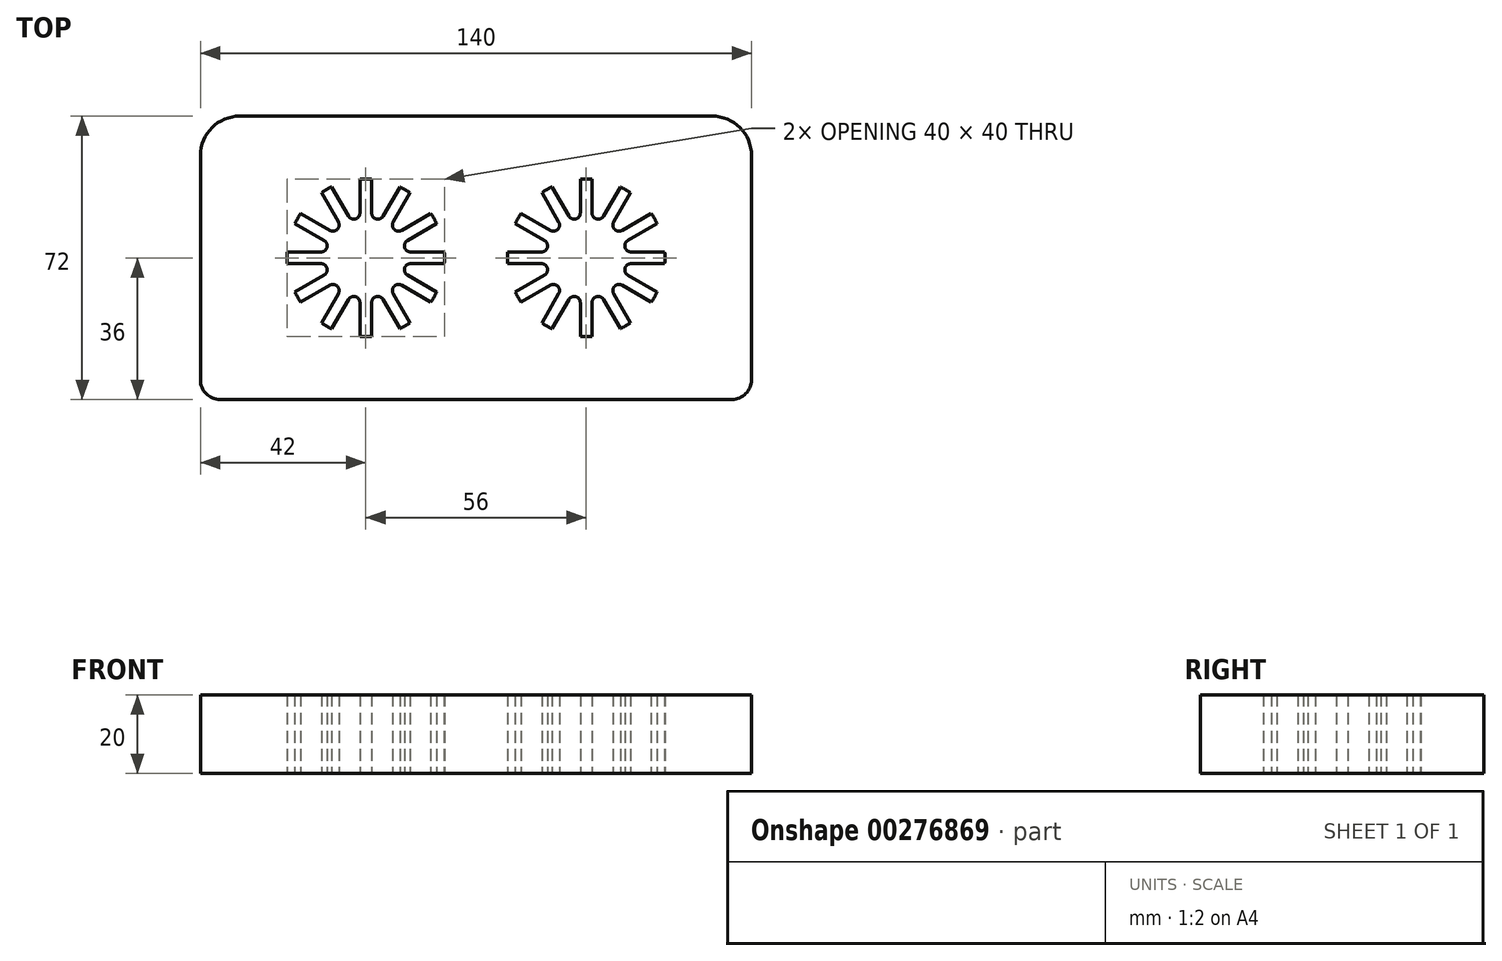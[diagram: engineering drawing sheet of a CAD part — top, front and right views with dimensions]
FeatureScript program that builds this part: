
annotation { "Feature Type Name" : "Feature", "Feature Type Description" : "" }
export const myFeature = defineFeature(function(context is Context, id is Id, definition is map)
    precondition{}
    {
        {
            var Q0;
            Q0=qCreatedBy(makeId("Top.planeOp"),FACE);
            var sketch = newSketch(context, id + "F0", { "sketchPlane" : qUnion([Q0])});
            skArc(sketch, "E0", {"start": v(-16.52, 11.27) * mm, "mid": v(-17.32, 10) * mm, "end": v(-18.02, 8.67) * mm});
            skArc(sketch, "E1", {"start": v(-6.35, 8) * mm, "mid": v(-7.23, 7.23) * mm, "end": v(-8, 6.35) * mm});
            skLineSegment(sketch, "E2", {"start": v(-19.94, -1.5) * mm, "end": v(-10.1, -1.5) * mm});
            skLineSegment(sketch, "E3", {"start": v(-20, 1.5) * mm, "end": v(-10.1, 1.5) * mm});
            skLineSegment(sketch, "E4", {"start": v(-18.02, 8.67) * mm, "end": v(-9.5, 3.76) * mm});
            skLineSegment(sketch, "E5", {"start": v(-16.52, 11.27) * mm, "end": v(-8, 6.35) * mm});
            skLineSegment(sketch, "E6", {"start": v(-1.5, 19.94) * mm, "end": v(-1.5, 10.1) * mm});
            skLineSegment(sketch, "E7", {"start": v(1.5, 19.94) * mm, "end": v(1.5, 10.1) * mm});
            skLineSegment(sketch, "E8", {"start": v(-8.42, 17.58) * mm, "end": v(-8.67, 18.02) * mm});
            skLineSegment(sketch, "E9", {"start": v(-8.67, 18.02) * mm, "end": v(-3.76, 9.5) * mm});
            skLineSegment(sketch, "E10", {"start": v(10.76, 15.64) * mm, "end": v(11.27, 16.52) * mm});
            skLineSegment(sketch, "E11", {"start": v(11.27, 16.52) * mm, "end": v(6.35, 8) * mm});
            skLineSegment(sketch, "E12", {"start": v(8.17, 17.14) * mm, "end": v(8.67, 18.02) * mm});
            skLineSegment(sketch, "E13", {"start": v(8.67, 18.02) * mm, "end": v(3.76, 9.5) * mm});
            skLineSegment(sketch, "E14", {"start": v(17.6, 8.43) * mm, "end": v(18.02, 8.67) * mm});
            skLineSegment(sketch, "E15", {"start": v(18.02, 8.67) * mm, "end": v(9.5, 3.76) * mm});
            skLineSegment(sketch, "E16", {"start": v(16.1, 11.03) * mm, "end": v(16.52, 11.27) * mm});
            skLineSegment(sketch, "E17", {"start": v(16.52, 11.27) * mm, "end": v(8, 6.35) * mm});
            skLineSegment(sketch, "E18", {"start": v(-10.8, 15.7) * mm, "end": v(-11.27, 16.52) * mm});
            skLineSegment(sketch, "E19", {"start": v(-10.8, 15.7) * mm, "end": v(-6.35, 8) * mm});
            skLineSegment(sketch, "E20.trimOffspring", {"start": v(-9.5, -3.76) * mm, "end": v(-18.02, -8.67) * mm});
            skLineSegment(sketch, "E21.trimOffspring", {"start": v(-8, -6.35) * mm, "end": v(-16.52, -11.27) * mm});
            skLineSegment(sketch, "E22.trimOffspring", {"start": v(-6.35, -8) * mm, "end": v(-11.27, -16.52) * mm});
            skLineSegment(sketch, "E23.trimOffspring", {"start": v(-3.76, -9.5) * mm, "end": v(-8.67, -18.02) * mm});
            skLineSegment(sketch, "E24.trimOffspring", {"start": v(-1.5, -10.1) * mm, "end": v(-1.5, -19.94) * mm});
            skLineSegment(sketch, "E25.trimOffspring", {"start": v(1.5, -10.1) * mm, "end": v(1.5, -19.94) * mm});
            skLineSegment(sketch, "E26.trimOffspring", {"start": v(3.76, -9.5) * mm, "end": v(8.67, -18.02) * mm});
            skLineSegment(sketch, "E27.trimOffspring", {"start": v(6.35, -8) * mm, "end": v(11.27, -16.52) * mm});
            skLineSegment(sketch, "E28.trimOffspring", {"start": v(8, -6.35) * mm, "end": v(16.52, -11.27) * mm});
            skLineSegment(sketch, "E29.trimOffspring", {"start": v(9.5, -3.76) * mm, "end": v(18.02, -8.67) * mm});
            skLineSegment(sketch, "E30.trimOffspring", {"start": v(10.1, -1.5) * mm, "end": v(19.94, -1.5) * mm});
            skLineSegment(sketch, "E31.trimOffspring", {"start": v(10.1, 1.5) * mm, "end": v(19.94, 1.5) * mm});
            skLineSegment(sketch, "E32", {"start": v(0, 0) * mm, "end": v(0, 20) * mm, "construction": true});
            skLineSegment(sketch, "E33", {"start": v(0, 0) * mm, "end": v(10, 17.32) * mm, "construction": true});
            skLineSegment(sketch, "E34", {"start": v(0, 0) * mm, "end": v(17.32, 10) * mm, "construction": true});
            skLineSegment(sketch, "E35", {"start": v(0, 0) * mm, "end": v(20, 0) * mm, "construction": true});
            skLineSegment(sketch, "E36", {"start": v(0, 0) * mm, "end": v(17.32, -10) * mm, "construction": true});
            skLineSegment(sketch, "E37", {"start": v(0, 0) * mm, "end": v(10, -17.32) * mm, "construction": true});
            skLineSegment(sketch, "E38", {"start": v(0, 0) * mm, "end": v(0, -20) * mm, "construction": true});
            skLineSegment(sketch, "E39", {"start": v(0, 0) * mm, "end": v(-10, -17.32) * mm, "construction": true});
            skLineSegment(sketch, "E40", {"start": v(0, 0) * mm, "end": v(-20, 0) * mm, "construction": true});
            skLineSegment(sketch, "E41", {"start": v(0, 0) * mm, "end": v(-17.32, 10) * mm, "construction": true});
            skLineSegment(sketch, "E42", {"start": v(0, 0) * mm, "end": v(-10, 17.32) * mm, "construction": true});
            skLineSegment(sketch, "E43", {"start": v(0, 0) * mm, "end": v(-17.32, -10) * mm, "construction": true});
            skArc(sketch, "E44.trimOffspring", {"start": v(-1.5, 10.1) * mm, "mid": v(-2.65, 9.87) * mm, "end": v(-3.76, 9.5) * mm});
            skArc(sketch, "E45.trimOffspring", {"start": v(3.76, 9.5) * mm, "mid": v(2.65, 9.87) * mm, "end": v(1.5, 10.1) * mm});
            skArc(sketch, "E46.trimOffspring", {"start": v(8, 6.35) * mm, "mid": v(7.23, 7.23) * mm, "end": v(6.35, 8) * mm});
            skArc(sketch, "E47.trimOffspring", {"start": v(10.1, 1.5) * mm, "mid": v(9.87, 2.65) * mm, "end": v(9.5, 3.76) * mm});
            skArc(sketch, "E48.trimOffspring", {"start": v(9.5, -3.76) * mm, "mid": v(9.87, -2.65) * mm, "end": v(10.1, -1.5) * mm});
            skArc(sketch, "E49.trimOffspring", {"start": v(6.35, -8) * mm, "mid": v(7.23, -7.23) * mm, "end": v(8, -6.35) * mm});
            skArc(sketch, "E50.trimOffspring", {"start": v(1.5, -10.1) * mm, "mid": v(2.65, -9.87) * mm, "end": v(3.76, -9.5) * mm});
            skArc(sketch, "E51.trimOffspring", {"start": v(-3.76, -9.5) * mm, "mid": v(-2.65, -9.87) * mm, "end": v(-1.5, -10.1) * mm});
            skArc(sketch, "E52.trimOffspring", {"start": v(-8, -6.35) * mm, "mid": v(-7.23, -7.23) * mm, "end": v(-6.35, -8) * mm});
            skArc(sketch, "E53.trimOffspring", {"start": v(-10.1, -1.5) * mm, "mid": v(-9.87, -2.65) * mm, "end": v(-9.5, -3.76) * mm});
            skArc(sketch, "E54.trimOffspring", {"start": v(-9.5, 3.76) * mm, "mid": v(-9.87, 2.65) * mm, "end": v(-10.1, 1.5) * mm});
            skArc(sketch, "E55.trimOffspring", {"start": v(-8.67, 18.02) * mm, "mid": v(-10, 17.32) * mm, "end": v(-11.27, 16.52) * mm});
            skArc(sketch, "E56.trimOffspring", {"start": v(1.5, 19.94) * mm, "mid": v(0, 20) * mm, "end": v(-1.5, 19.94) * mm});
            skArc(sketch, "E57.trimOffspring", {"start": v(11.27, 16.52) * mm, "mid": v(10, 17.32) * mm, "end": v(8.67, 18.02) * mm});
            skArc(sketch, "E58.trimOffspring", {"start": v(18.02, 8.67) * mm, "mid": v(17.32, 10) * mm, "end": v(16.52, 11.27) * mm});
            skArc(sketch, "E59.trimOffspring", {"start": v(19.94, -1.5) * mm, "mid": v(20, 0) * mm, "end": v(19.94, 1.5) * mm});
            skArc(sketch, "E60.trimOffspring", {"start": v(16.52, -11.27) * mm, "mid": v(17.32, -10) * mm, "end": v(18.02, -8.67) * mm});
            skArc(sketch, "E61.trimOffspring", {"start": v(8.67, -18.02) * mm, "mid": v(10, -17.32) * mm, "end": v(11.27, -16.52) * mm});
            skArc(sketch, "E62.trimOffspring", {"start": v(-1.5, -19.94) * mm, "mid": v(0, -20) * mm, "end": v(1.5, -19.94) * mm});
            skArc(sketch, "E63.trimOffspring", {"start": v(-11.27, -16.52) * mm, "mid": v(-10, -17.32) * mm, "end": v(-8.67, -18.02) * mm});
            skArc(sketch, "E64.trimOffspring", {"start": v(-18.02, -8.67) * mm, "mid": v(-17.32, -10) * mm, "end": v(-16.52, -11.27) * mm});
            skArc(sketch, "E65.trimOffspring", {"start": v(-19.94, 1.5) * mm, "mid": v(-20, 0) * mm, "end": v(-19.94, -1.5) * mm});
            skArc(sketch, "E66", {"start": v(-72.52, 11.27) * mm, "mid": v(-73.32, 10) * mm, "end": v(-74.02, 8.67) * mm});
            skArc(sketch, "E67", {"start": v(-62.35, 8) * mm, "mid": v(-63.23, 7.23) * mm, "end": v(-64, 6.35) * mm});
            skLineSegment(sketch, "E68", {"start": v(-75.94, -1.5) * mm, "end": v(-66.1, -1.5) * mm});
            skLineSegment(sketch, "E69", {"start": v(-76, 1.5) * mm, "end": v(-66.1, 1.5) * mm});
            skLineSegment(sketch, "E70", {"start": v(-74.02, 8.67) * mm, "end": v(-65.5, 3.76) * mm});
            skLineSegment(sketch, "E71", {"start": v(-72.52, 11.27) * mm, "end": v(-64, 6.35) * mm});
            skLineSegment(sketch, "E72", {"start": v(-57.5, 19.94) * mm, "end": v(-57.5, 10.1) * mm});
            skLineSegment(sketch, "E73", {"start": v(-54.5, 19.94) * mm, "end": v(-54.5, 10.1) * mm});
            skLineSegment(sketch, "E74", {"start": v(-64.42, 17.58) * mm, "end": v(-64.67, 18.02) * mm});
            skLineSegment(sketch, "E75", {"start": v(-64.67, 18.02) * mm, "end": v(-59.76, 9.5) * mm});
            skLineSegment(sketch, "E76", {"start": v(-45.24, 15.64) * mm, "end": v(-44.73, 16.52) * mm});
            skLineSegment(sketch, "E77", {"start": v(-44.73, 16.52) * mm, "end": v(-49.65, 8) * mm});
            skLineSegment(sketch, "E78", {"start": v(-47.83, 17.14) * mm, "end": v(-47.33, 18.02) * mm});
            skLineSegment(sketch, "E79", {"start": v(-47.33, 18.02) * mm, "end": v(-52.24, 9.5) * mm});
            skLineSegment(sketch, "E80", {"start": v(-38.4, 8.43) * mm, "end": v(-37.98, 8.67) * mm});
            skLineSegment(sketch, "E81", {"start": v(-37.98, 8.67) * mm, "end": v(-46.5, 3.76) * mm});
            skLineSegment(sketch, "E82", {"start": v(-39.9, 11.03) * mm, "end": v(-39.48, 11.27) * mm});
            skLineSegment(sketch, "E83", {"start": v(-39.48, 11.27) * mm, "end": v(-48, 6.35) * mm});
            skLineSegment(sketch, "E84", {"start": v(-66.8, 15.7) * mm, "end": v(-67.27, 16.52) * mm});
            skLineSegment(sketch, "E85", {"start": v(-66.8, 15.7) * mm, "end": v(-62.35, 8) * mm});
            skLineSegment(sketch, "E86.trimOffspring", {"start": v(-65.5, -3.76) * mm, "end": v(-74.02, -8.67) * mm});
            skLineSegment(sketch, "E87.trimOffspring", {"start": v(-64, -6.35) * mm, "end": v(-72.52, -11.27) * mm});
            skLineSegment(sketch, "E88.trimOffspring", {"start": v(-62.35, -8) * mm, "end": v(-67.27, -16.52) * mm});
            skLineSegment(sketch, "E89.trimOffspring", {"start": v(-59.76, -9.5) * mm, "end": v(-64.67, -18.02) * mm});
            skLineSegment(sketch, "E90.trimOffspring", {"start": v(-57.5, -10.1) * mm, "end": v(-57.5, -19.94) * mm});
            skLineSegment(sketch, "E91.trimOffspring", {"start": v(-54.5, -10.1) * mm, "end": v(-54.5, -19.94) * mm});
            skLineSegment(sketch, "E92.trimOffspring", {"start": v(-52.24, -9.5) * mm, "end": v(-47.33, -18.02) * mm});
            skLineSegment(sketch, "E93.trimOffspring", {"start": v(-49.65, -8) * mm, "end": v(-44.73, -16.52) * mm});
            skLineSegment(sketch, "E94.trimOffspring", {"start": v(-48, -6.35) * mm, "end": v(-39.48, -11.27) * mm});
            skLineSegment(sketch, "E95.trimOffspring", {"start": v(-46.5, -3.76) * mm, "end": v(-37.98, -8.67) * mm});
            skLineSegment(sketch, "E96.trimOffspring", {"start": v(-45.9, -1.5) * mm, "end": v(-36.06, -1.5) * mm});
            skLineSegment(sketch, "E97.trimOffspring", {"start": v(-45.9, 1.5) * mm, "end": v(-36.06, 1.5) * mm});
            skLineSegment(sketch, "E98", {"start": v(-56, 0) * mm, "end": v(-56, 20) * mm, "construction": true});
            skLineSegment(sketch, "E99", {"start": v(-56, 0) * mm, "end": v(-46, 17.32) * mm, "construction": true});
            skLineSegment(sketch, "E100", {"start": v(-56, 0) * mm, "end": v(-38.68, 10) * mm, "construction": true});
            skLineSegment(sketch, "E101", {"start": v(-56, 0) * mm, "end": v(-36, 0) * mm, "construction": true});
            skLineSegment(sketch, "E102", {"start": v(-56, 0) * mm, "end": v(-38.68, -10) * mm, "construction": true});
            skLineSegment(sketch, "E103", {"start": v(-56, 0) * mm, "end": v(-46, -17.32) * mm, "construction": true});
            skLineSegment(sketch, "E104", {"start": v(-56, 0) * mm, "end": v(-56, -20) * mm, "construction": true});
            skLineSegment(sketch, "E105", {"start": v(-56, 0) * mm, "end": v(-66, -17.32) * mm, "construction": true});
            skLineSegment(sketch, "E106", {"start": v(-56, 0) * mm, "end": v(-76, 0) * mm, "construction": true});
            skLineSegment(sketch, "E107", {"start": v(-56, 0) * mm, "end": v(-73.32, 10) * mm, "construction": true});
            skLineSegment(sketch, "E108", {"start": v(-56, 0) * mm, "end": v(-66, 17.32) * mm, "construction": true});
            skLineSegment(sketch, "E109", {"start": v(-56, 0) * mm, "end": v(-73.32, -10) * mm, "construction": true});
            skArc(sketch, "E110.trimOffspring", {"start": v(-57.5, 10.1) * mm, "mid": v(-58.65, 9.87) * mm, "end": v(-59.76, 9.5) * mm});
            skArc(sketch, "E111.trimOffspring", {"start": v(-52.24, 9.5) * mm, "mid": v(-53.35, 9.87) * mm, "end": v(-54.5, 10.1) * mm});
            skArc(sketch, "E112.trimOffspring", {"start": v(-48, 6.35) * mm, "mid": v(-48.77, 7.23) * mm, "end": v(-49.65, 8) * mm});
            skArc(sketch, "E113.trimOffspring", {"start": v(-45.9, 1.5) * mm, "mid": v(-46.13, 2.65) * mm, "end": v(-46.5, 3.76) * mm});
            skArc(sketch, "E114.trimOffspring", {"start": v(-46.5, -3.76) * mm, "mid": v(-46.13, -2.65) * mm, "end": v(-45.9, -1.5) * mm});
            skArc(sketch, "E115.trimOffspring", {"start": v(-49.65, -8) * mm, "mid": v(-48.77, -7.23) * mm, "end": v(-48, -6.35) * mm});
            skArc(sketch, "E116.trimOffspring", {"start": v(-54.5, -10.1) * mm, "mid": v(-53.35, -9.87) * mm, "end": v(-52.24, -9.5) * mm});
            skArc(sketch, "E117.trimOffspring", {"start": v(-59.76, -9.5) * mm, "mid": v(-58.65, -9.87) * mm, "end": v(-57.5, -10.1) * mm});
            skArc(sketch, "E118.trimOffspring", {"start": v(-64, -6.35) * mm, "mid": v(-63.23, -7.23) * mm, "end": v(-62.35, -8) * mm});
            skArc(sketch, "E119.trimOffspring", {"start": v(-66.1, -1.5) * mm, "mid": v(-65.87, -2.65) * mm, "end": v(-65.5, -3.76) * mm});
            skArc(sketch, "E120.trimOffspring", {"start": v(-65.5, 3.76) * mm, "mid": v(-65.87, 2.65) * mm, "end": v(-66.1, 1.5) * mm});
            skArc(sketch, "E121.trimOffspring", {"start": v(-64.67, 18.02) * mm, "mid": v(-66, 17.32) * mm, "end": v(-67.27, 16.52) * mm});
            skArc(sketch, "E122.trimOffspring", {"start": v(-54.5, 19.94) * mm, "mid": v(-56, 20) * mm, "end": v(-57.5, 19.94) * mm});
            skArc(sketch, "E123.trimOffspring", {"start": v(-44.73, 16.52) * mm, "mid": v(-46, 17.32) * mm, "end": v(-47.33, 18.02) * mm});
            skArc(sketch, "E124.trimOffspring", {"start": v(-37.98, 8.67) * mm, "mid": v(-38.68, 10) * mm, "end": v(-39.48, 11.27) * mm});
            skArc(sketch, "E125.trimOffspring", {"start": v(-36.06, -1.5) * mm, "mid": v(-36, 0) * mm, "end": v(-36.06, 1.5) * mm});
            skArc(sketch, "E126.trimOffspring", {"start": v(-39.48, -11.27) * mm, "mid": v(-38.68, -10) * mm, "end": v(-37.98, -8.67) * mm});
            skArc(sketch, "E127.trimOffspring", {"start": v(-47.33, -18.02) * mm, "mid": v(-46, -17.32) * mm, "end": v(-44.73, -16.52) * mm});
            skArc(sketch, "E128.trimOffspring", {"start": v(-57.5, -19.94) * mm, "mid": v(-56, -20) * mm, "end": v(-54.5, -19.94) * mm});
            skArc(sketch, "E129.trimOffspring", {"start": v(-67.27, -16.52) * mm, "mid": v(-66, -17.32) * mm, "end": v(-64.67, -18.02) * mm});
            skArc(sketch, "E130.trimOffspring", {"start": v(-74.02, -8.67) * mm, "mid": v(-73.32, -10) * mm, "end": v(-72.52, -11.27) * mm});
            skArc(sketch, "E131.trimOffspring", {"start": v(-75.94, 1.5) * mm, "mid": v(-76, 0) * mm, "end": v(-75.94, -1.5) * mm});
            skLineSegment(sketch, "E132", {"start": v(42, -31) * mm, "end": v(42, 26) * mm});
            skLineSegment(sketch, "E133", {"start": v(32, 36) * mm, "end": v(-88, 36) * mm});
            skLineSegment(sketch, "E134", {"start": v(-98, 26) * mm, "end": v(-98, -31) * mm});
            skPoint(sketch, "E135.visualSharp", {"position": v(-98, 36) * mm});
            skArc(sketch, "E135.filletArc", {"start": v(-88, 36) * mm, "mid": v(-95.07, 33.07) * mm, "end": v(-98, 26) * mm});
            skPoint(sketch, "E136.visualSharp", {"position": v(42, 36) * mm});
            skArc(sketch, "E136.filletArc", {"start": v(42, 26) * mm, "mid": v(39.07, 33.07) * mm, "end": v(32, 36) * mm});
            skPoint(sketch, "E137.visualSharp", {"position": v(-98, -36) * mm});
            skArc(sketch, "E137.filletArc", {"start": v(-98, -31) * mm, "mid": v(-96.54, -34.54) * mm, "end": v(-93, -36) * mm});
            skPoint(sketch, "E138.visualSharp", {"position": v(42, -36) * mm});
            skArc(sketch, "E138.filletArc", {"start": v(37, -36) * mm, "mid": v(40.54, -34.54) * mm, "end": v(42, -31) * mm});
            skLineSegment(sketch, "E139", {"start": v(-93, -36) * mm, "end": v(37, -36) * mm});
            skSolve(sketch);
        }
        {
            var Q0;
            Q0=qSketchRegion(id+"F0",true);
            extrude(context, id + "F1", {"entities" : qUnion([Q0]), "depth" : 20 * mm});
        }
        {
            var Q0;
            Q0=makeQuery(id+"F1.opExtrude","SWEPT_EDGE",EDGE,{"disambiguationData":[OSD([sQuery(id+"F0.wireOp",EDGE,"E9"),sQuery(id+"F0.wireOp",EDGE,"E44.trimOffspring")])]});
            var Q1;
            Q1=makeQuery(id+"F1.opExtrude","SWEPT_EDGE",EDGE,{"disambiguationData":[OSD([sQuery(id+"F0.wireOp",EDGE,"E6"),sQuery(id+"F0.wireOp",EDGE,"E44.trimOffspring")])]});
            var Q2;
            Q2=makeQuery(id+"F1.opExtrude","SWEPT_EDGE",EDGE,{"disambiguationData":[OSD([sQuery(id+"F0.wireOp",EDGE,"E13"),sQuery(id+"F0.wireOp",EDGE,"E45.trimOffspring")])]});
            var Q3;
            Q3=makeQuery(id+"F1.opExtrude","SWEPT_EDGE",EDGE,{"disambiguationData":[OSD([sQuery(id+"F0.wireOp",EDGE,"E7"),sQuery(id+"F0.wireOp",EDGE,"E45.trimOffspring")])]});
            var Q4;
            Q4=makeQuery(id+"F1.opExtrude","SWEPT_EDGE",EDGE,{"disambiguationData":[OSD([sQuery(id+"F0.wireOp",EDGE,"E11"),sQuery(id+"F0.wireOp",EDGE,"E46.trimOffspring")])]});
            var Q5;
            Q5=makeQuery(id+"F1.opExtrude","SWEPT_EDGE",EDGE,{"disambiguationData":[OSD([sQuery(id+"F0.wireOp",EDGE,"E17"),sQuery(id+"F0.wireOp",EDGE,"E46.trimOffspring")])]});
            var Q6;
            Q6=makeQuery(id+"F1.opExtrude","SWEPT_EDGE",EDGE,{"disambiguationData":[OSD([sQuery(id+"F0.wireOp",EDGE,"E15"),sQuery(id+"F0.wireOp",EDGE,"E47.trimOffspring")])]});
            var Q7;
            Q7=makeQuery(id+"F1.opExtrude","SWEPT_EDGE",EDGE,{"disambiguationData":[OSD([sQuery(id+"F0.wireOp",EDGE,"E31.trimOffspring"),sQuery(id+"F0.wireOp",EDGE,"E47.trimOffspring")])]});
            var Q8;
            Q8=makeQuery(id+"F1.opExtrude","SWEPT_EDGE",EDGE,{"disambiguationData":[OSD([sQuery(id+"F0.wireOp",EDGE,"E30.trimOffspring"),sQuery(id+"F0.wireOp",EDGE,"E48.trimOffspring")])]});
            var Q9;
            Q9=makeQuery(id+"F1.opExtrude","SWEPT_EDGE",EDGE,{"disambiguationData":[OSD([sQuery(id+"F0.wireOp",EDGE,"E29.trimOffspring"),sQuery(id+"F0.wireOp",EDGE,"E48.trimOffspring")])]});
            var Q10;
            Q10=makeQuery(id+"F1.opExtrude","SWEPT_EDGE",EDGE,{"disambiguationData":[OSD([sQuery(id+"F0.wireOp",EDGE,"E28.trimOffspring"),sQuery(id+"F0.wireOp",EDGE,"E49.trimOffspring")])]});
            var Q11;
            Q11=makeQuery(id+"F1.opExtrude","SWEPT_EDGE",EDGE,{"disambiguationData":[OSD([sQuery(id+"F0.wireOp",EDGE,"E27.trimOffspring"),sQuery(id+"F0.wireOp",EDGE,"E49.trimOffspring")])]});
            var Q12;
            Q12=makeQuery(id+"F1.opExtrude","SWEPT_EDGE",EDGE,{"disambiguationData":[OSD([sQuery(id+"F0.wireOp",EDGE,"E26.trimOffspring"),sQuery(id+"F0.wireOp",EDGE,"E50.trimOffspring")])]});
            var Q13;
            Q13=makeQuery(id+"F1.opExtrude","SWEPT_EDGE",EDGE,{"disambiguationData":[OSD([sQuery(id+"F0.wireOp",EDGE,"E25.trimOffspring"),sQuery(id+"F0.wireOp",EDGE,"E50.trimOffspring")])]});
            var Q14;
            Q14=makeQuery(id+"F1.opExtrude","SWEPT_EDGE",EDGE,{"disambiguationData":[OSD([sQuery(id+"F0.wireOp",EDGE,"E23.trimOffspring"),sQuery(id+"F0.wireOp",EDGE,"E51.trimOffspring")])]});
            var Q15;
            Q15=makeQuery(id+"F1.opExtrude","SWEPT_EDGE",EDGE,{"disambiguationData":[OSD([sQuery(id+"F0.wireOp",EDGE,"E24.trimOffspring"),sQuery(id+"F0.wireOp",EDGE,"E51.trimOffspring")])]});
            var Q16;
            Q16=makeQuery(id+"F1.opExtrude","SWEPT_EDGE",EDGE,{"disambiguationData":[OSD([sQuery(id+"F0.wireOp",EDGE,"E21.trimOffspring"),sQuery(id+"F0.wireOp",EDGE,"E52.trimOffspring")])]});
            var Q17;
            Q17=makeQuery(id+"F1.opExtrude","SWEPT_EDGE",EDGE,{"disambiguationData":[OSD([sQuery(id+"F0.wireOp",EDGE,"E22.trimOffspring"),sQuery(id+"F0.wireOp",EDGE,"E52.trimOffspring")])]});
            var Q18;
            Q18=makeQuery(id+"F1.opExtrude","SWEPT_EDGE",EDGE,{"disambiguationData":[OSD([sQuery(id+"F0.wireOp",EDGE,"E2"),sQuery(id+"F0.wireOp",EDGE,"E53.trimOffspring")])]});
            var Q19;
            Q19=makeQuery(id+"F1.opExtrude","SWEPT_EDGE",EDGE,{"disambiguationData":[OSD([sQuery(id+"F0.wireOp",EDGE,"E20.trimOffspring"),sQuery(id+"F0.wireOp",EDGE,"E53.trimOffspring")])]});
            var Q20;
            Q20=makeQuery(id+"F1.opExtrude","SWEPT_EDGE",EDGE,{"disambiguationData":[OSD([sQuery(id+"F0.wireOp",EDGE,"E4"),sQuery(id+"F0.wireOp",EDGE,"E54.trimOffspring")])]});
            var Q21;
            Q21=makeQuery(id+"F1.opExtrude","SWEPT_EDGE",EDGE,{"disambiguationData":[OSD([sQuery(id+"F0.wireOp",EDGE,"E3"),sQuery(id+"F0.wireOp",EDGE,"E54.trimOffspring")])]});
            var Q22;
            Q22=makeQuery(id+"F1.opExtrude","SWEPT_EDGE",EDGE,{"disambiguationData":[OSD([sQuery(id+"F0.wireOp",EDGE,"E67"),sQuery(id+"F0.wireOp",EDGE,"E85")])]});
            var Q23;
            Q23=makeQuery(id+"F1.opExtrude","SWEPT_EDGE",EDGE,{"disambiguationData":[OSD([sQuery(id+"F0.wireOp",EDGE,"E67"),sQuery(id+"F0.wireOp",EDGE,"E71")])]});
            var Q24;
            Q24=makeQuery(id+"F1.opExtrude","SWEPT_EDGE",EDGE,{"disambiguationData":[OSD([sQuery(id+"F0.wireOp",EDGE,"E75"),sQuery(id+"F0.wireOp",EDGE,"E110.trimOffspring")])]});
            var Q25;
            Q25=makeQuery(id+"F1.opExtrude","SWEPT_EDGE",EDGE,{"disambiguationData":[OSD([sQuery(id+"F0.wireOp",EDGE,"E72"),sQuery(id+"F0.wireOp",EDGE,"E110.trimOffspring")])]});
            var Q26;
            Q26=makeQuery(id+"F1.opExtrude","SWEPT_EDGE",EDGE,{"disambiguationData":[OSD([sQuery(id+"F0.wireOp",EDGE,"E79"),sQuery(id+"F0.wireOp",EDGE,"E111.trimOffspring")])]});
            var Q27;
            Q27=makeQuery(id+"F1.opExtrude","SWEPT_EDGE",EDGE,{"disambiguationData":[OSD([sQuery(id+"F0.wireOp",EDGE,"E83"),sQuery(id+"F0.wireOp",EDGE,"E112.trimOffspring")])]});
            var Q28;
            Q28=makeQuery(id+"F1.opExtrude","SWEPT_EDGE",EDGE,{"disambiguationData":[OSD([sQuery(id+"F0.wireOp",EDGE,"E73"),sQuery(id+"F0.wireOp",EDGE,"E111.trimOffspring")])]});
            var Q29;
            Q29=makeQuery(id+"F1.opExtrude","SWEPT_EDGE",EDGE,{"disambiguationData":[OSD([sQuery(id+"F0.wireOp",EDGE,"E77"),sQuery(id+"F0.wireOp",EDGE,"E112.trimOffspring")])]});
            var Q30;
            Q30=makeQuery(id+"F1.opExtrude","SWEPT_EDGE",EDGE,{"disambiguationData":[OSD([sQuery(id+"F0.wireOp",EDGE,"E97.trimOffspring"),sQuery(id+"F0.wireOp",EDGE,"E113.trimOffspring")])]});
            var Q31;
            Q31=makeQuery(id+"F1.opExtrude","SWEPT_EDGE",EDGE,{"disambiguationData":[OSD([sQuery(id+"F0.wireOp",EDGE,"E81"),sQuery(id+"F0.wireOp",EDGE,"E113.trimOffspring")])]});
            var Q32;
            Q32=makeQuery(id+"F1.opExtrude","SWEPT_EDGE",EDGE,{"disambiguationData":[OSD([sQuery(id+"F0.wireOp",EDGE,"E70"),sQuery(id+"F0.wireOp",EDGE,"E120.trimOffspring")])]});
            var Q33;
            Q33=makeQuery(id+"F1.opExtrude","SWEPT_EDGE",EDGE,{"disambiguationData":[OSD([sQuery(id+"F0.wireOp",EDGE,"E86.trimOffspring"),sQuery(id+"F0.wireOp",EDGE,"E119.trimOffspring")])]});
            var Q34;
            Q34=makeQuery(id+"F1.opExtrude","SWEPT_EDGE",EDGE,{"disambiguationData":[OSD([sQuery(id+"F0.wireOp",EDGE,"E68"),sQuery(id+"F0.wireOp",EDGE,"E119.trimOffspring")])]});
            var Q35;
            Q35=makeQuery(id+"F1.opExtrude","SWEPT_EDGE",EDGE,{"disambiguationData":[OSD([sQuery(id+"F0.wireOp",EDGE,"E69"),sQuery(id+"F0.wireOp",EDGE,"E120.trimOffspring")])]});
            var Q36;
            Q36=makeQuery(id+"F1.opExtrude","SWEPT_EDGE",EDGE,{"disambiguationData":[OSD([sQuery(id+"F0.wireOp",EDGE,"E87.trimOffspring"),sQuery(id+"F0.wireOp",EDGE,"E118.trimOffspring")])]});
            var Q37;
            Q37=makeQuery(id+"F1.opExtrude","SWEPT_EDGE",EDGE,{"disambiguationData":[OSD([sQuery(id+"F0.wireOp",EDGE,"E88.trimOffspring"),sQuery(id+"F0.wireOp",EDGE,"E118.trimOffspring")])]});
            var Q38;
            Q38=makeQuery(id+"F1.opExtrude","SWEPT_EDGE",EDGE,{"disambiguationData":[OSD([sQuery(id+"F0.wireOp",EDGE,"E89.trimOffspring"),sQuery(id+"F0.wireOp",EDGE,"E117.trimOffspring")])]});
            var Q39;
            Q39=makeQuery(id+"F1.opExtrude","SWEPT_EDGE",EDGE,{"disambiguationData":[OSD([sQuery(id+"F0.wireOp",EDGE,"E90.trimOffspring"),sQuery(id+"F0.wireOp",EDGE,"E117.trimOffspring")])]});
            var Q40;
            Q40=makeQuery(id+"F1.opExtrude","SWEPT_EDGE",EDGE,{"disambiguationData":[OSD([sQuery(id+"F0.wireOp",EDGE,"E92.trimOffspring"),sQuery(id+"F0.wireOp",EDGE,"E116.trimOffspring")])]});
            var Q41;
            Q41=makeQuery(id+"F1.opExtrude","SWEPT_EDGE",EDGE,{"disambiguationData":[OSD([sQuery(id+"F0.wireOp",EDGE,"E91.trimOffspring"),sQuery(id+"F0.wireOp",EDGE,"E116.trimOffspring")])]});
            var Q42;
            Q42=makeQuery(id+"F1.opExtrude","SWEPT_EDGE",EDGE,{"disambiguationData":[OSD([sQuery(id+"F0.wireOp",EDGE,"E93.trimOffspring"),sQuery(id+"F0.wireOp",EDGE,"E115.trimOffspring")])]});
            var Q43;
            Q43=makeQuery(id+"F1.opExtrude","SWEPT_EDGE",EDGE,{"disambiguationData":[OSD([sQuery(id+"F0.wireOp",EDGE,"E94.trimOffspring"),sQuery(id+"F0.wireOp",EDGE,"E115.trimOffspring")])]});
            var Q44;
            Q44=makeQuery(id+"F1.opExtrude","SWEPT_EDGE",EDGE,{"disambiguationData":[OSD([sQuery(id+"F0.wireOp",EDGE,"E95.trimOffspring"),sQuery(id+"F0.wireOp",EDGE,"E114.trimOffspring")])]});
            var Q45;
            Q45=makeQuery(id+"F1.opExtrude","SWEPT_EDGE",EDGE,{"disambiguationData":[OSD([sQuery(id+"F0.wireOp",EDGE,"E96.trimOffspring"),sQuery(id+"F0.wireOp",EDGE,"E114.trimOffspring")])]});
            var Q46;
            Q46=makeQuery(id+"F1.opExtrude","SWEPT_EDGE",EDGE,{"disambiguationData":[OSD([sQuery(id+"F0.wireOp",EDGE,"E1"),sQuery(id+"F0.wireOp",EDGE,"E19")])]});
            var Q47;
            Q47=makeQuery(id+"F1.opExtrude","SWEPT_EDGE",EDGE,{"disambiguationData":[OSD([sQuery(id+"F0.wireOp",EDGE,"E1"),sQuery(id+"F0.wireOp",EDGE,"E5")])]});
            fillet(context, id + "F2", {"entities" : qUnion([Q0, Q1, Q2, Q3, Q4, Q5, Q6, Q7, Q8, Q9, Q10, Q11, Q12, Q13, Q14, Q15, Q16, Q17, Q18, Q19, Q20, Q21, Q22, Q23, Q24, Q25, Q26, Q27, Q28, Q29, Q30, Q31, Q32, Q33, Q34, Q35, Q36, Q37, Q38, Q39, Q40, Q41, Q42, Q43, Q44, Q45, Q46, Q47]), "radius" : 1.5 * mm, "tangentPropagation" : true, "allowEdgeOverflow" : false});
        }
    });
